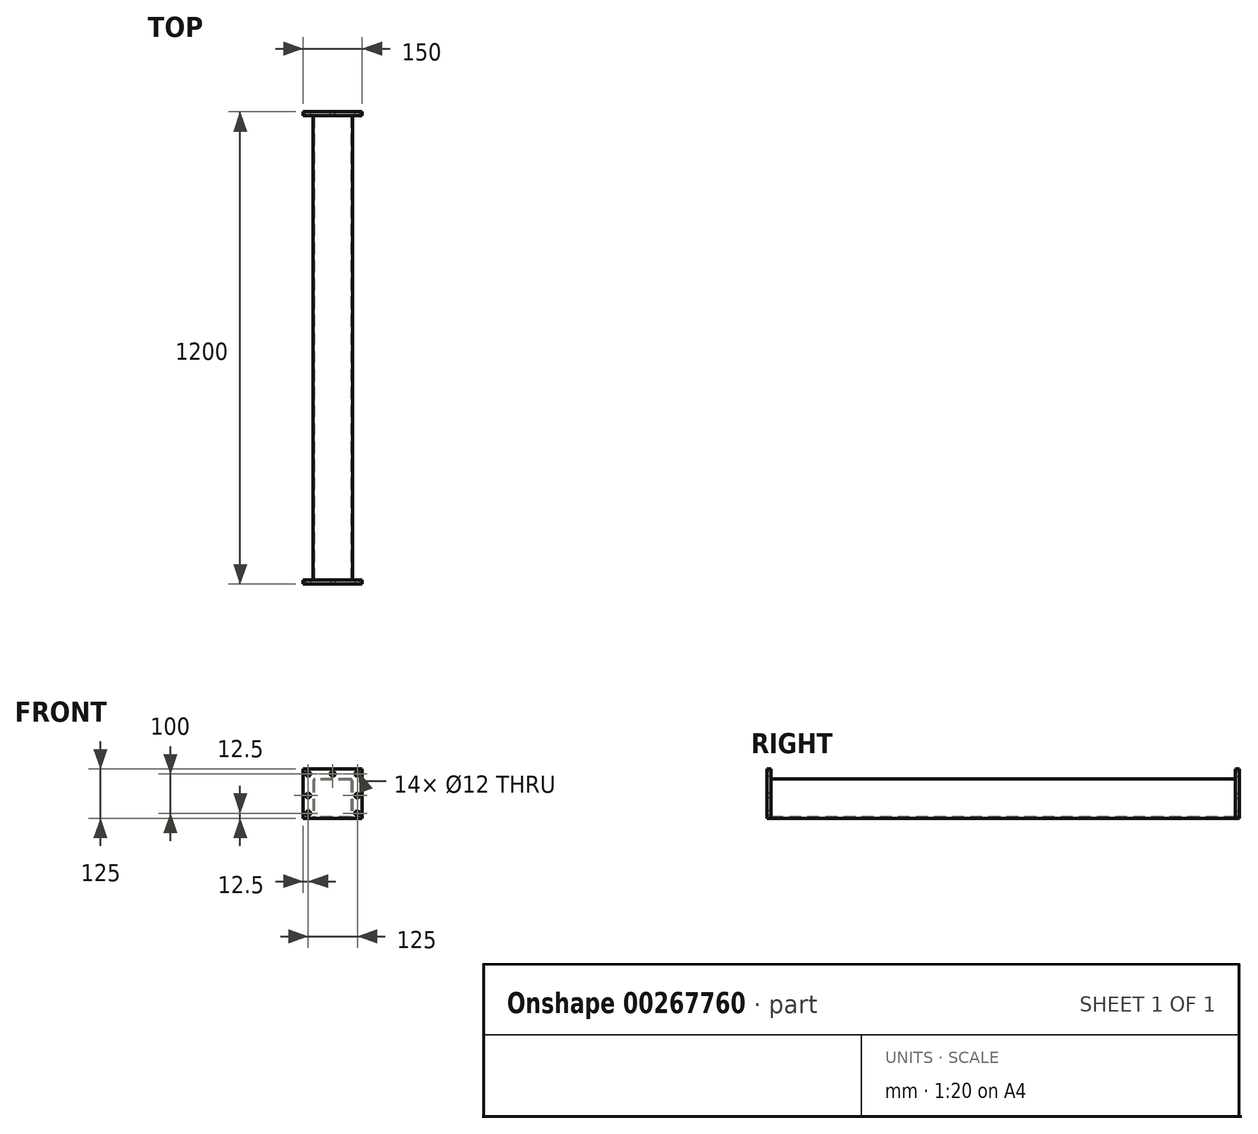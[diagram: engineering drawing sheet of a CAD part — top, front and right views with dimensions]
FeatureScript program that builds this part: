
annotation { "Feature Type Name" : "Feature", "Feature Type Description" : "" }
export const myFeature = defineFeature(function(context is Context, id is Id, definition is map)
    precondition{}
    {
        {
            var Q0;
            Q0=qCreatedBy(makeId("Front.planeOp"),FACE);
            var sketch = newSketch(context, id + "F0", { "sketchPlane" : qUnion([Q0])});
            skLineSegment(sketch, "E0.bottom", {"start": v(45, 50) * mm, "end": v(-45, 50) * mm});
            skLineSegment(sketch, "E0.top", {"start": v(45, -50) * mm, "end": v(-45, -50) * mm});
            skLineSegment(sketch, "E0.left", {"start": v(50, 45) * mm, "end": v(50, -45) * mm});
            skLineSegment(sketch, "E0.right", {"start": v(-50, 45) * mm, "end": v(-50, -45) * mm});
            skPoint(sketch, "E0.middle", {"position": v(0, 0) * mm});
            skPoint(sketch, "E1.visualSharp", {"position": v(-50, 50) * mm});
            skArc(sketch, "E1.filletArc", {"start": v(-45, 50) * mm, "mid": v(-48.54, 48.54) * mm, "end": v(-50, 45) * mm});
            skPoint(sketch, "E2.visualSharp", {"position": v(50, 50) * mm});
            skArc(sketch, "E2.filletArc", {"start": v(50, 45) * mm, "mid": v(48.54, 48.54) * mm, "end": v(45, 50) * mm});
            skPoint(sketch, "E3.visualSharp", {"position": v(50, -50) * mm});
            skArc(sketch, "E3.filletArc", {"start": v(45, -50) * mm, "mid": v(48.54, -48.54) * mm, "end": v(50, -45) * mm});
            skPoint(sketch, "E4.visualSharp", {"position": v(-50, -50) * mm});
            skArc(sketch, "E4.filletArc", {"start": v(-50, -45) * mm, "mid": v(-48.54, -48.54) * mm, "end": v(-45, -50) * mm});
            skArc(sketch, "E5.0", {"start": v(-45, 47) * mm, "mid": v(-46.41, 46.41) * mm, "end": v(-47, 45) * mm});
            skLineSegment(sketch, "E5.1", {"start": v(45, 47) * mm, "end": v(-45, 47) * mm});
            skLineSegment(sketch, "E5.2", {"start": v(-47, 45) * mm, "end": v(-47, -45) * mm});
            skArc(sketch, "E5.3", {"start": v(47, 45) * mm, "mid": v(46.41, 46.41) * mm, "end": v(45, 47) * mm});
            skArc(sketch, "E5.4", {"start": v(-47, -45) * mm, "mid": v(-46.41, -46.41) * mm, "end": v(-45, -47) * mm});
            skLineSegment(sketch, "E5.5", {"start": v(45, -47) * mm, "end": v(-45, -47) * mm});
            skArc(sketch, "E5.6", {"start": v(45, -47) * mm, "mid": v(46.41, -46.41) * mm, "end": v(47, -45) * mm});
            skLineSegment(sketch, "E5.7", {"start": v(47, 45) * mm, "end": v(47, -45) * mm});
            skSolve(sketch);
        }
        {
            var Q0;
            Q0=makeQuery(id+"F0.imprint","IMPRINT",FACE,{"disambiguationData":[TD([[makeQuery(id+"F0.imprint","IMPRINT",EDGE,{"derivedFrom":sQuery(id+"F0.wireOp",EDGE,"E0.bottom")}),1.0]])]});
            extrude(context, id + "F1", {"entities" : qUnion([Q0]), "oppositeDirection" : true, "depth" : 1180 * mm});
        }
        {
            var Q0;
            Q0=makeQuery(id+"F1.opExtrude","CAP_FACE",FACE,{"disambiguationData":[OSD([sQuery(id+"F0.wireOp",EDGE,"E0.bottom"),sQuery(id+"F0.wireOp",EDGE,"E0.top"),sQuery(id+"F0.wireOp",EDGE,"E0.left"),sQuery(id+"F0.wireOp",EDGE,"E0.right"),sQuery(id+"F0.wireOp",EDGE,"E1.filletArc"),sQuery(id+"F0.wireOp",EDGE,"E2.filletArc"),sQuery(id+"F0.wireOp",EDGE,"E3.filletArc"),sQuery(id+"F0.wireOp",EDGE,"E4.filletArc"),sQuery(id+"F0.wireOp",EDGE,"E5.0"),sQuery(id+"F0.wireOp",EDGE,"E5.1"),sQuery(id+"F0.wireOp",EDGE,"E5.2"),sQuery(id+"F0.wireOp",EDGE,"E5.3"),sQuery(id+"F0.wireOp",EDGE,"E5.4"),sQuery(id+"F0.wireOp",EDGE,"E5.5"),sQuery(id+"F0.wireOp",EDGE,"E5.6"),sQuery(id+"F0.wireOp",EDGE,"E5.7")])],"isStart":true});
            cPlane(context, id + "F2", {"entities" : qUnion([Q0]), "cplaneType" : CPlaneType.OFFSET, "offset" : 10 * mm, "width" : 150 * mm, "height" : 150 * mm});
        }
        {
            var Q0;
            Q0=qCreatedBy(id+"F2.planeOp",FACE);
            var sketch = newSketch(context, id + "F3", { "sketchPlane" : qUnion([Q0])});
            skLineSegment(sketch, "E6.bottom", {"start": v(-75, 75) * mm, "end": v(75, 75) * mm});
            skLineSegment(sketch, "E6.top", {"start": v(-75, -50) * mm, "end": v(75, -50) * mm});
            skLineSegment(sketch, "E6.left", {"start": v(-75, 75) * mm, "end": v(-75, -50) * mm});
            skLineSegment(sketch, "E6.right", {"start": v(75, 75) * mm, "end": v(75, -50) * mm});
            skCircle(sketch, "E7", {"center": v(-62.5, -37.5) * mm, "radius": 6 * mm});
            skCircle(sketch, "E8", {"center": v(-62.5, 7.5) * mm, "radius": 6 * mm});
            skCircle(sketch, "E9", {"center": v(62.5, 7.5) * mm, "radius": 6 * mm});
            skCircle(sketch, "E10", {"center": v(62.5, -37.5) * mm, "radius": 6 * mm});
            skCircle(sketch, "E11", {"center": v(-62.5, 62.5) * mm, "radius": 6 * mm});
            skCircle(sketch, "E12", {"center": v(62.5, 62.5) * mm, "radius": 6 * mm});
            skCircle(sketch, "E13", {"center": v(0, 62.5) * mm, "radius": 6 * mm});
            skSolve(sketch);
        }
        {
            var Q0;
            Q0=makeQuery(id+"F3.imprint","IMPRINT",FACE,{"disambiguationData":[TD([[makeQuery(id+"F3.imprint","IMPRINT",EDGE,{"derivedFrom":sQuery(id+"F3.wireOp",EDGE,"E6.bottom")}),-1.0]])]});
            extrude(context, id + "F4", {"entities" : qUnion([Q0]), "oppositeDirection" : true, "depth" : 10 * mm});
        }
        {
            var Q0;
            Q0=makeQuery(id+"F1.opExtrude","SWEPT_BODY",BODY,{"disambiguationData":[OSD([sQuery(id+"F0.wireOp",EDGE,"E0.bottom"),sQuery(id+"F0.wireOp",EDGE,"E0.top"),sQuery(id+"F0.wireOp",EDGE,"E0.left"),sQuery(id+"F0.wireOp",EDGE,"E0.right"),sQuery(id+"F0.wireOp",EDGE,"E1.filletArc"),sQuery(id+"F0.wireOp",EDGE,"E2.filletArc"),sQuery(id+"F0.wireOp",EDGE,"E3.filletArc"),sQuery(id+"F0.wireOp",EDGE,"E4.filletArc"),sQuery(id+"F0.wireOp",EDGE,"E5.0"),sQuery(id+"F0.wireOp",EDGE,"E5.1"),sQuery(id+"F0.wireOp",EDGE,"E5.2"),sQuery(id+"F0.wireOp",EDGE,"E5.3"),sQuery(id+"F0.wireOp",EDGE,"E5.4"),sQuery(id+"F0.wireOp",EDGE,"E5.5"),sQuery(id+"F0.wireOp",EDGE,"E5.6"),sQuery(id+"F0.wireOp",EDGE,"E5.7")])]});
            var Q1;
            Q1=makeQuery(id+"F4.opExtrude","SWEPT_BODY",BODY,{"disambiguationData":[OSD([sQuery(id+"F3.wireOp",EDGE,"E6.bottom"),sQuery(id+"F3.wireOp",EDGE,"E6.top"),sQuery(id+"F3.wireOp",EDGE,"E6.left"),sQuery(id+"F3.wireOp",EDGE,"E6.right")])]});
            booleanBodies(context, id + "F5", {"operationType" : BooleanOperationType.UNION, "tools" : qUnion([Q0, Q1])});
        }
        {
            var Q0;
            Q0=makeQuery(id+"F1.opExtrude","CAP_FACE",FACE,{"disambiguationData":[OSD([sQuery(id+"F0.wireOp",EDGE,"E0.bottom"),sQuery(id+"F0.wireOp",EDGE,"E0.top"),sQuery(id+"F0.wireOp",EDGE,"E0.left"),sQuery(id+"F0.wireOp",EDGE,"E0.right"),sQuery(id+"F0.wireOp",EDGE,"E1.filletArc"),sQuery(id+"F0.wireOp",EDGE,"E2.filletArc"),sQuery(id+"F0.wireOp",EDGE,"E3.filletArc"),sQuery(id+"F0.wireOp",EDGE,"E4.filletArc"),sQuery(id+"F0.wireOp",EDGE,"E5.0"),sQuery(id+"F0.wireOp",EDGE,"E5.1"),sQuery(id+"F0.wireOp",EDGE,"E5.2"),sQuery(id+"F0.wireOp",EDGE,"E5.3"),sQuery(id+"F0.wireOp",EDGE,"E5.4"),sQuery(id+"F0.wireOp",EDGE,"E5.5"),sQuery(id+"F0.wireOp",EDGE,"E5.6"),sQuery(id+"F0.wireOp",EDGE,"E5.7")])],"isStart":false});
            cPlane(context, id + "F6", {"entities" : qUnion([Q0]), "cplaneType" : CPlaneType.OFFSET, "offset" : 10 * mm, "width" : 150 * mm, "height" : 150 * mm});
        }
        {
            var Q0;
            Q0=qCreatedBy(id+"F6.planeOp",FACE);
            var sketch = newSketch(context, id + "F7", { "sketchPlane" : qUnion([Q0])});
            skLineSegment(sketch, "E14.bottom", {"start": v(-75, 75) * mm, "end": v(75, 75) * mm});
            skLineSegment(sketch, "E14.top", {"start": v(-75, -50) * mm, "end": v(75, -50) * mm});
            skLineSegment(sketch, "E14.left", {"start": v(-75, 75) * mm, "end": v(-75, -50) * mm});
            skLineSegment(sketch, "E14.right", {"start": v(75, 75) * mm, "end": v(75, -50) * mm});
            skCircle(sketch, "E15", {"center": v(-62.5, -37.5) * mm, "radius": 6 * mm});
            skCircle(sketch, "E16", {"center": v(-62.5, 7.5) * mm, "radius": 6 * mm});
            skCircle(sketch, "E17", {"center": v(62.5, 7.5) * mm, "radius": 6 * mm});
            skCircle(sketch, "E18", {"center": v(62.5, -37.5) * mm, "radius": 6 * mm});
            skCircle(sketch, "E19", {"center": v(-62.5, 62.5) * mm, "radius": 6 * mm});
            skCircle(sketch, "E20", {"center": v(62.5, 62.5) * mm, "radius": 6 * mm});
            skCircle(sketch, "E21", {"center": v(0, 62.5) * mm, "radius": 6 * mm});
            skSolve(sketch);
        }
        {
            var Q0;
            Q0 = qSketchRegion(id + "F7", true);
            extrude(context, id + "F8", {"entities" : qUnion([Q0]), "operationType" : NewBodyOperationType.ADD, "oppositeDirection" : true, "depth" : 10 * mm});
        }
    });
